# Revit family: 201_KHA-_
name_source: partatom
category: Air Terminals
units: mm (PartAtom-declared; Revit-internal decimal feet)

## family parameters
Always vertical = Yes
Cut with Voids When Loaded = No
Part Type = Normal
Room Calculation Point = Yes
Round Connector Dimension = Use Diameter
Shared = No
Work Plane-Based = No

## types (7) — shared parameters
CAT0 = Yes
CL_Location_5000 = 5000 mm  [stored 16.4042 ft]
Description = SUPPLY AIR JET
L_ARR = 400 mm  [stored 1.31234 ft]
Manufacturer = Alnor
QmdConnectorList = 201;D
URL = http://www.ventilation-alnor.co.uk
W_ARR = 400 mm  [stored 1.31234 ft]
XRefLineVPlnId = 7453
YRefLineVPlnId = 7456
magiPartTypeId = 201
magiProductFamilyId = KHA-*
zero-valued in all types: CLBTZ, H_ARR

## per-type parameters (varying)
| type | AX | D | D3 | G1 | G1__ve | R |
| KHA-100 | 8 mm  [stored 0.0262467 ft] | 100 mm | 162 mm  [stored 0.531496 ft] | 54 mm | -54 mm | 50 mm  [stored 0.164042 ft] |
| KHA-400 | 71 mm | 400 mm | 483 mm | 159 mm | -159 mm | 200 mm  [stored 0.656168 ft] |
| KHA-315 | 52 mm | 315 mm | 400 mm  [stored 1.31234 ft] | 133 mm | -133 mm | 158 mm |
| KHA-250 | 39 mm | 250 mm | 318 mm | 114 mm | -114 mm | 125 mm  [stored 0.410105 ft] |
| KHA-200 | 30 mm  [stored 0.0984252 ft] | 200 mm | 273 mm | 89 mm | -89 mm | 100 mm  [stored 0.328084 ft] |
| KHA-160 | 26 mm | 160 mm | 216 mm | 76 mm | -76 mm | 80 mm |
| KHA-125 | 14 mm  [stored 0.0459318 ft] | 125 mm | 185 mm | 63 mm | -63 mm | 63 mm |

note: column(s) folded — value = type name in every type: MC Product Code, magiProductId

note: [stored X ft] marks values corroborated as IEEE doubles in the binary element streams (Revit-internal decimal feet)

## geometry (parser evidence)
native form markers: Blend x2, Sweep x2
no freeform markers — native parametric forms only
